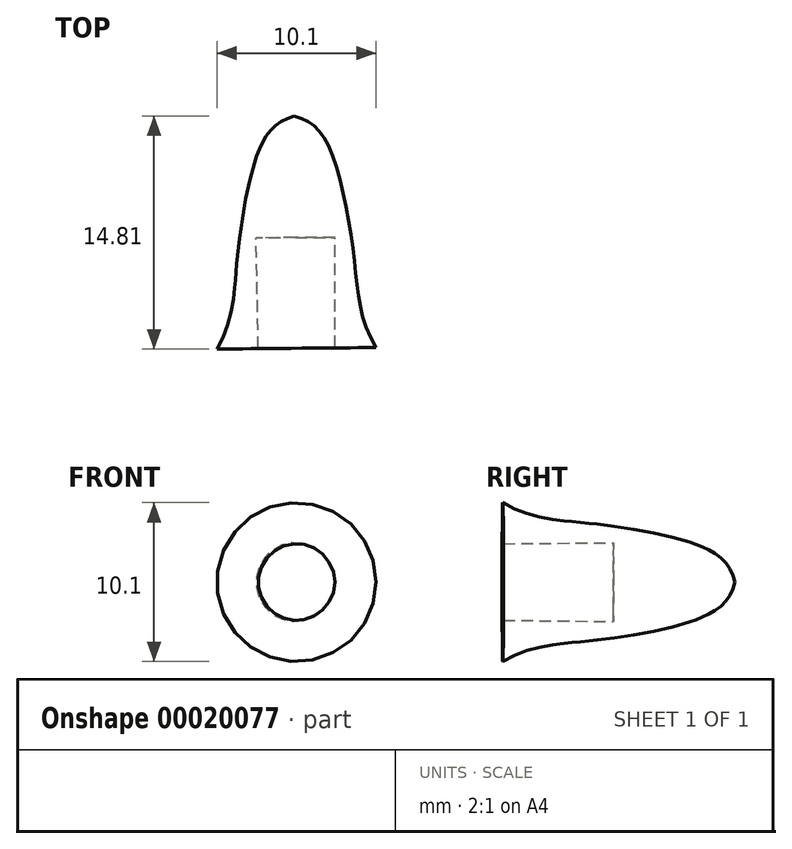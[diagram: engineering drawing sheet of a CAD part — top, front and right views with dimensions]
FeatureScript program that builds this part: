
annotation { "Feature Type Name" : "Feature", "Feature Type Description" : "" }
export const myFeature = defineFeature(function(context is Context, id is Id, definition is map)
    precondition{}
    {
        {
            var Q0;
            Q0=qCreatedBy(makeId("Top.planeOp"),FACE);
            var sketch = newSketch(context, id + "F0", { "sketchPlane" : qUnion([Q0])});
            skLineSegment(sketch, "E0.bottom", {"start": v(2.5, 0) * mm, "end": v(5.12, 0) * mm});
            skLineSegment(sketch, "E0.left", {"start": v(0, 7) * mm, "end": v(-0.08, 14.7) * mm});
            skFitSpline(sketch, "E1", {"points": [v(-0.08, 14.7) * mm, v(1.94, 13.12) * mm, v(3.73, 5.62) * mm, v(5.12, 0) * mm], "startDerivative": vector(11.39, -3.3) * mm, "endDerivative": vector(9.36, -15.44) * mm});
            skLineSegment(sketch, "E2.top", {"start": v(0, 7) * mm, "end": v(2.5, 7) * mm});
            skLineSegment(sketch, "E2.right", {"start": v(2.5, 0) * mm, "end": v(2.5, 7) * mm});
            skSolve(sketch);
        }
        {
            var Q0;
            Q0 = qSketchRegion(id + "F0", true);
            var Q1;
            Q1=sQuery(id+"F0.wireOp",EDGE,"E0.left");
            revolve(context, id + "F1", {"entities" : qUnion([Q0]), "axis" : qUnion([Q1]), "revolveType" : RevolveType.FULL});
        }
    });
